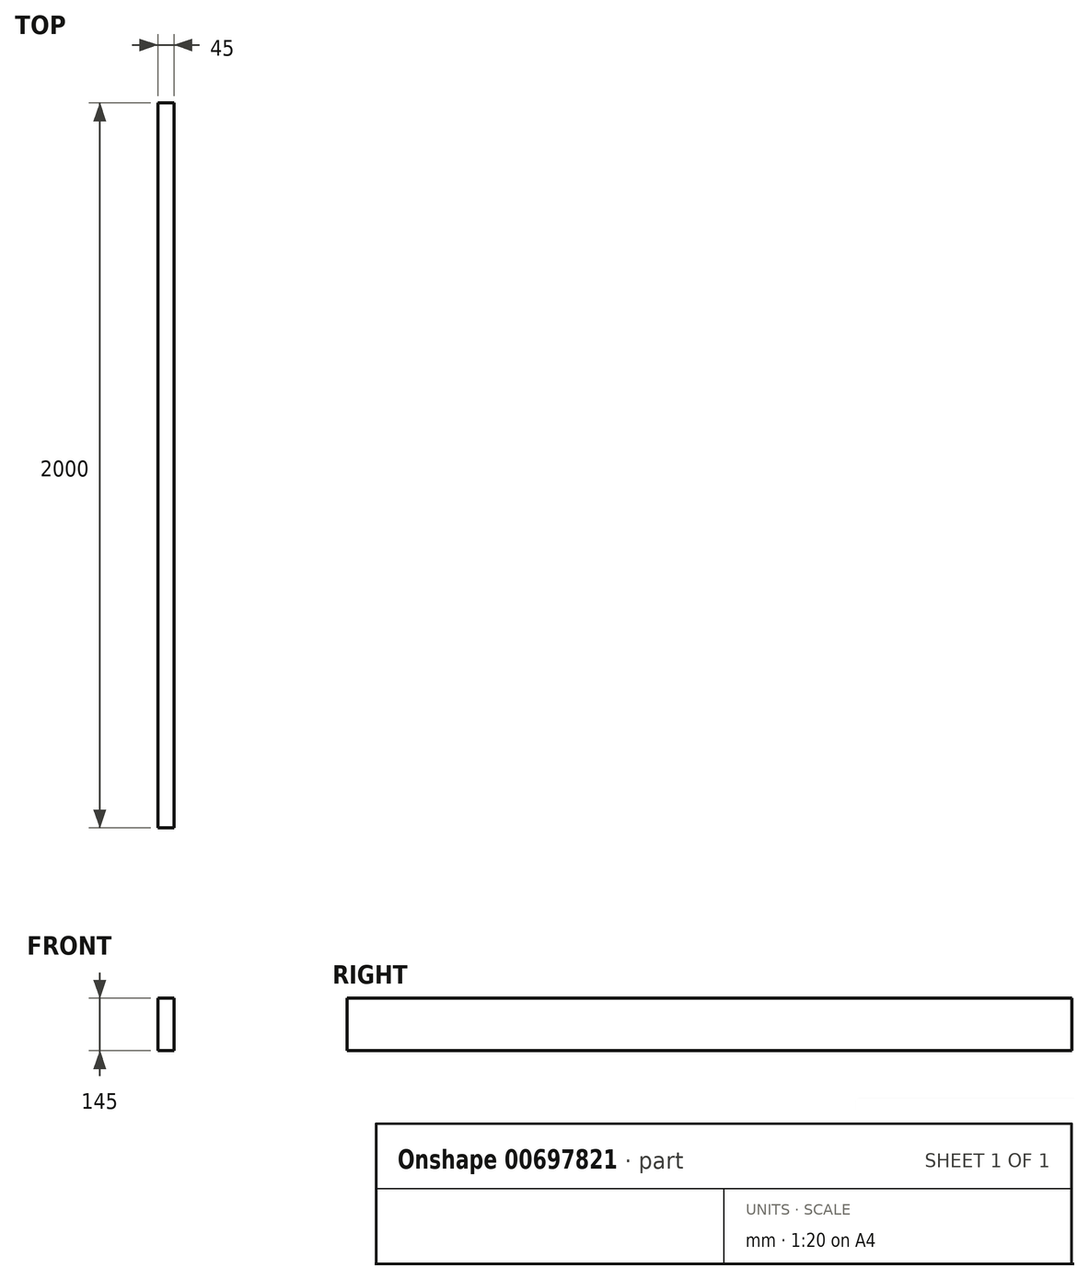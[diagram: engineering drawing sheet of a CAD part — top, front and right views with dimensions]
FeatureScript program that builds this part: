
annotation { "Feature Type Name" : "Feature", "Feature Type Description" : "" }
export const myFeature = defineFeature(function(context is Context, id is Id, definition is map)
    precondition{}
    {
        {
            var Q0;
            Q0=qCreatedBy(makeId("Front.planeOp"),FACE);
            var sketch = newSketch(context, id + "F0", { "sketchPlane" : qUnion([Q0])});
            skLineSegment(sketch, "E0.bottom", {"start": v(-260.57, 145) * mm, "end": v(-215.57, 145) * mm});
            skLineSegment(sketch, "E0.top", {"start": v(-260.57, 0) * mm, "end": v(-215.57, 0) * mm});
            skLineSegment(sketch, "E0.left", {"start": v(-260.57, 145) * mm, "end": v(-260.57, 0) * mm});
            skLineSegment(sketch, "E0.right", {"start": v(-215.57, 145) * mm, "end": v(-215.57, 0) * mm});
            skSolve(sketch);
        }
        {
            var Q0;
            Q0=makeQuery(id+"F0.imprint","IMPRINT",FACE,{"disambiguationData":[TD([[makeQuery(id+"F0.imprint","IMPRINT",EDGE,{"derivedFrom":sQuery(id+"F0.wireOp",EDGE,"E0.bottom")}),-1.0]])]});
            extrude(context, id + "F1", {"entities" : qUnion([Q0]), "oppositeDirection" : true, "depth" : 2000 * mm, "offsetDistance" : 25 * mm});
        }
    });
